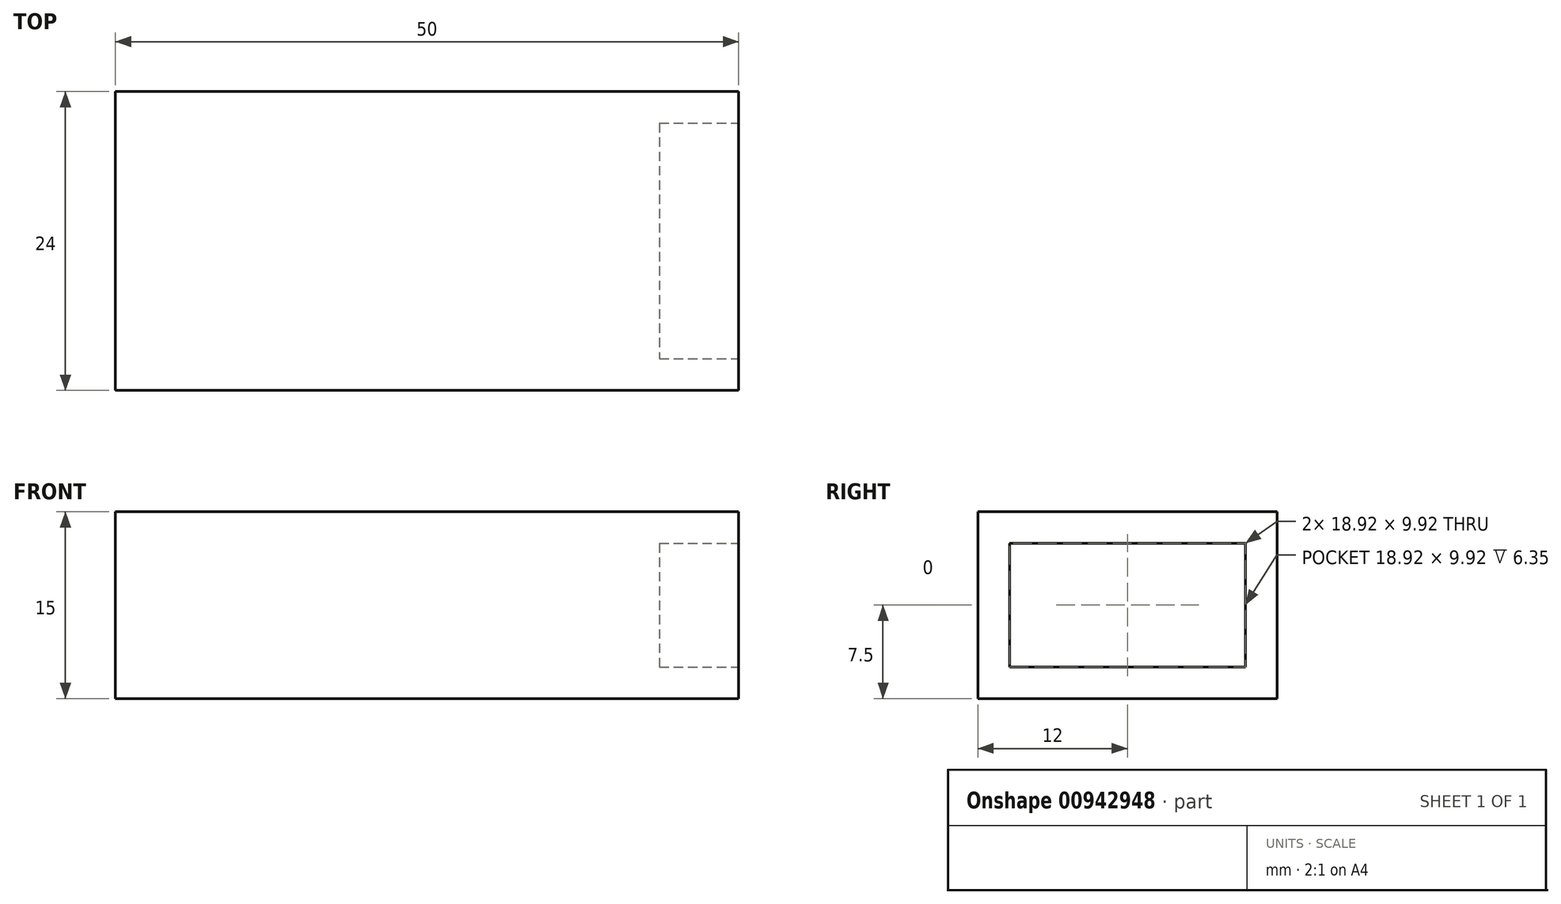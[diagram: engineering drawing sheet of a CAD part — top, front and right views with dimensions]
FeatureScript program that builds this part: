
annotation { "Feature Type Name" : "Feature", "Feature Type Description" : "" }
export const myFeature = defineFeature(function(context is Context, id is Id, definition is map)
    precondition{}
    {
        {
            var Q0;
            Q0=qCreatedBy(makeId("Top.planeOp"),FACE);
            var sketch = newSketch(context, id + "F0", { "sketchPlane" : qUnion([Q0])});
            skLineSegment(sketch, "E0", {"start": v(-25, 0) * mm, "end": v(-25, -12) * mm});
            skLineSegment(sketch, "E1.MirrorCS", {"start": v(-25, 0) * mm, "end": v(-25, 12) * mm});
            skLineSegment(sketch, "E2.MirrorCS", {"start": v(25, 0) * mm, "end": v(25, 12) * mm});
            skLineSegment(sketch, "E3.MirrorCS", {"start": v(25, 0) * mm, "end": v(25, -12) * mm});
            skLineSegment(sketch, "E4", {"start": v(-25, 12) * mm, "end": v(25, 12) * mm});
            skLineSegment(sketch, "E5", {"start": v(25, -12) * mm, "end": v(-25, -12) * mm});
            skSolve(sketch);
        }
        {
            var Q0;
            Q0=makeQuery(id+"F0.imprint","IMPRINT",FACE,{"disambiguationData":[TD([[makeQuery(id+"F0.imprint","IMPRINT",EDGE,{"derivedFrom":sQuery(id+"F0.wireOp",EDGE,"E0")}),1.0]])]});
            extrude(context, id + "F1", {"entities" : qUnion([Q0]), "depth" : 15 * mm, "offsetDistance" : 25.4 * mm});
        }
        {
            var Q0;
            Q0=makeQuery(id+"F1.opExtrude","SWEPT_FACE",FACE,{"disambiguationData":[OSD([sQuery(id+"F0.wireOp",EDGE,"E2.MirrorCS"),sQuery(id+"F0.wireOp",EDGE,"E3.MirrorCS")])]});
            var sketch = newSketch(context, id + "F2", { "sketchPlane" : qUnion([Q0])});
            skLineSegment(sketch, "E6.MirrorCS", {"start": v(12, 0) * mm, "end": v(12, 2.54) * mm});
            skLineSegment(sketch, "E7.MirrorCS", {"start": v(12, 15) * mm, "end": v(12, 12.46) * mm});
            skLineSegment(sketch, "E8", {"start": v(-9.46, 12.46) * mm, "end": v(-9.46, 2.54) * mm});
            skLineSegment(sketch, "E9", {"start": v(-9.46, 2.54) * mm, "end": v(9.46, 2.54) * mm});
            skLineSegment(sketch, "E10", {"start": v(9.46, 12.46) * mm, "end": v(9.46, 2.54) * mm});
            skLineSegment(sketch, "E11", {"start": v(9.46, 12.46) * mm, "end": v(-9.46, 12.46) * mm});
            skPoint(sketch, "E12.MirrorCS.start.orphan", {"position": v(12, 2.54) * mm});
            skPoint(sketch, "E13.end.orphan", {"position": v(-12, 2.54) * mm});
            skPoint(sketch, "E13.start.orphan", {"position": v(-12, 0) * mm});
            skSolve(sketch);
        }
        {
            var Q0;
            Q0=makeQuery(id+"F2.imprint","IMPRINT",FACE,{"disambiguationData":[TD([[makeQuery(id+"F2.imprint","IMPRINT",EDGE,{"derivedFrom":sQuery(id+"F2.wireOp",EDGE,"E8")}),1.0]])]});
            extrude(context, id + "F3", {"entities" : qUnion([Q0]), "operationType" : NewBodyOperationType.REMOVE, "oppositeDirection" : true, "depth" : 6.35 * mm, "offsetDistance" : 25.4 * mm});
        }
    });
